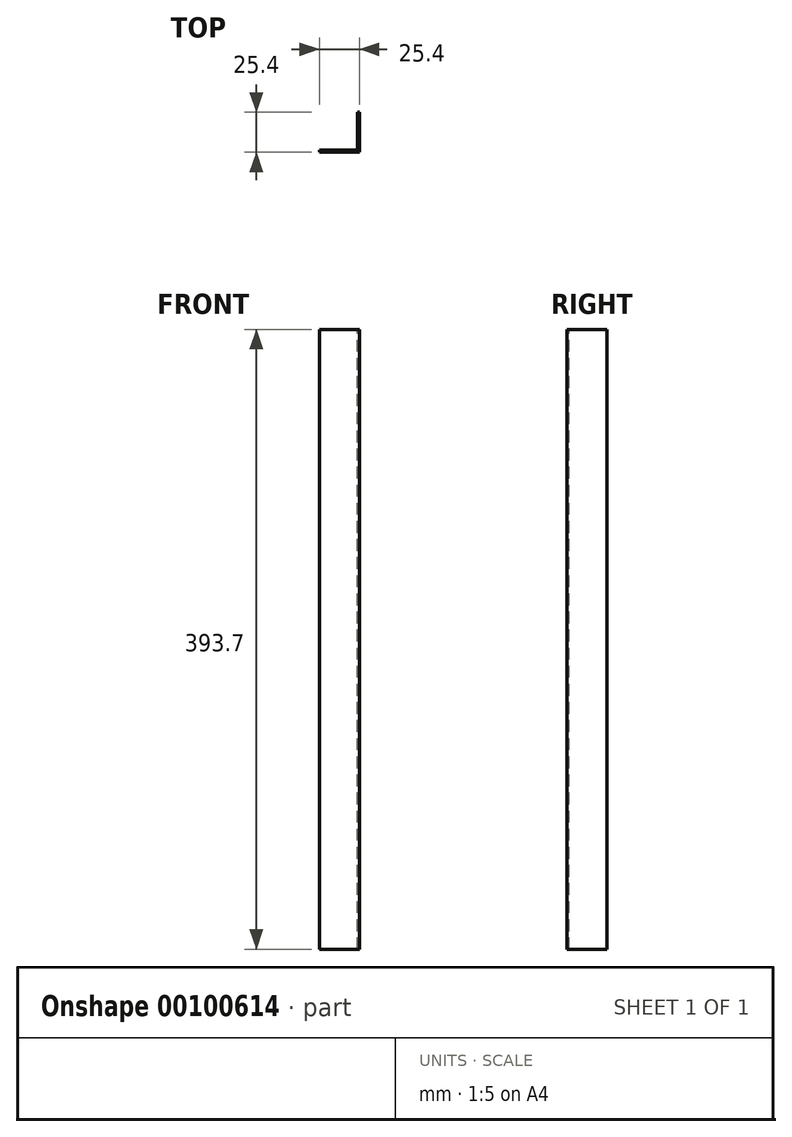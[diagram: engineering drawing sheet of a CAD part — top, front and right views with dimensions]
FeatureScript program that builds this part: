
annotation { "Feature Type Name" : "Feature", "Feature Type Description" : "" }
export const myFeature = defineFeature(function(context is Context, id is Id, definition is map)
    precondition{}
    {
        {
            var Q0;
            Q0=qCreatedBy(makeId("Top.planeOp"),FACE);
            var sketch = newSketch(context, id + "F0", { "sketchPlane" : qUnion([Q0])});
            skLineSegment(sketch, "E0", {"start": v(-25.4, 0) * mm, "end": v(0, 0) * mm});
            skLineSegment(sketch, "E1", {"start": v(0, 0) * mm, "end": v(0, 25.4) * mm});
            skLineSegment(sketch, "E2.0", {"start": v(-1.27, 1.27) * mm, "end": v(-1.27, 25.4) * mm});
            skLineSegment(sketch, "E2.1", {"start": v(-25.4, 1.27) * mm, "end": v(-1.27, 1.27) * mm});
            skLineSegment(sketch, "E3", {"start": v(-25.4, 0) * mm, "end": v(-25.4, 1.27) * mm});
            skLineSegment(sketch, "E4", {"start": v(0, 25.4) * mm, "end": v(-1.27, 25.4) * mm});
            skSolve(sketch);
        }
        {
            var Q0;
            Q0=makeQuery(id+"F0.imprint","IMPRINT",FACE,{"disambiguationData":[TD([[makeQuery(id+"F0.imprint","IMPRINT",EDGE,{"derivedFrom":sQuery(id+"F0.wireOp",EDGE,"E0")}),1.0]])]});
            extrude(context, id + "F1", {"entities" : qUnion([Q0]), "oppositeDirection" : true, "depth" : 393.7 * mm});
        }
    });
